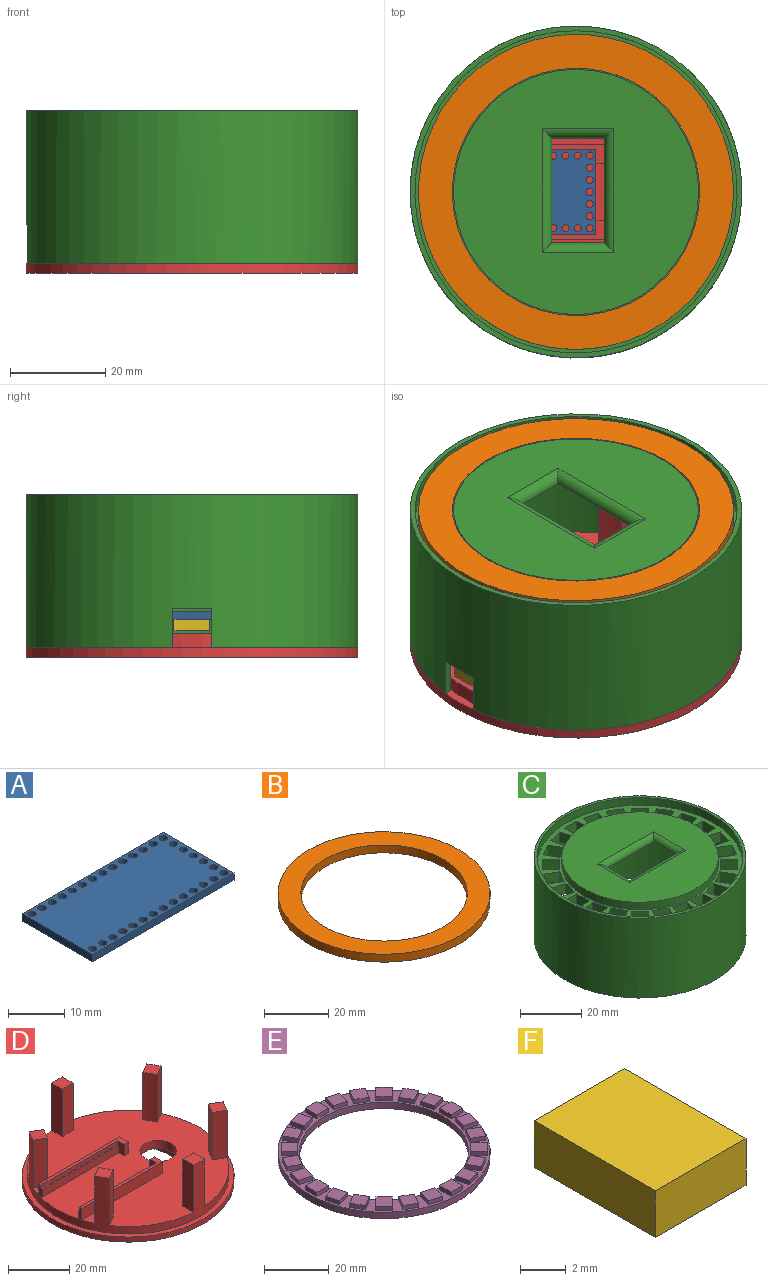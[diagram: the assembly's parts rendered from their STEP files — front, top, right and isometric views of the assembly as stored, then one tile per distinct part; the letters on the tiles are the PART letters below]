
ASSEMBLY  parts=6 mates=9
PART A: 39 faces, bbox 35.6x17.8x1.6 mm
  f0: plane 35.56x1.57mm, normal (0,1,0), area 55.8mm2, adj f1,f3,f4,f5
  f1: plane 17.78x1.57mm, normal (-1,0,0), area 27.9mm2, adj f0,f2,f4,f5
  f2: plane 35.56x1.57mm, normal (0,-1,0), area 55.8mm2, adj f1,f3,f4,f5
  f3: plane 17.78x1.57mm, normal (1,0,0), area 27.9mm2, adj f0,f2,f4,f5
  f4: plane 35.56x17.78mm, normal (0,0,1), area 573.9mm2, adj f0,f1,f2,f3,f6,f7,f8,f9
  f5: plane 35.56x17.78mm, normal (0,0,-1), area 573.9mm2, adj f0,f1,f2,f3,f6,f7,f8,f9
  f6: cylinder r=0.75mm len=1.57mm, axis (0,0,1), area 7.4mm2, adj f4,f5
  f7: cylinder r=0.75mm len=1.57mm, axis (0,0,1), area 7.4mm2, adj f4,f5
  f8: cylinder r=0.75mm len=1.57mm, axis (0,0,1), area 7.4mm2, adj f4,f5
  f9: cylinder r=0.75mm len=1.57mm, axis (0,0,1), area 7.4mm2, adj f4,f5
  f10: cylinder r=0.75mm len=1.57mm, axis (0,0,1), area 7.4mm2, adj f4,f5
  f11: cylinder r=0.75mm len=1.57mm, axis (0,0,1), area 7.4mm2, adj f4,f5
  f12: cylinder r=0.75mm len=1.57mm, axis (0,0,1), area 7.4mm2, adj f4,f5
  f13: cylinder r=0.75mm len=1.57mm, axis (0,0,1), area 7.4mm2, adj f4,f5
  f14: cylinder r=0.75mm len=1.57mm, axis (0,0,1), area 7.4mm2, adj f4,f5
  f15: cylinder r=0.75mm len=1.57mm, axis (0,0,1), area 7.4mm2, adj f4,f5
  f16: cylinder r=0.75mm len=1.57mm, axis (0,0,1), area 7.4mm2, adj f4,f5
  f17: cylinder r=0.75mm len=1.57mm, axis (0,0,1), area 7.4mm2, adj f4,f5
  f18: cylinder r=0.75mm len=1.57mm, axis (0,0,1), area 7.4mm2, adj f4,f5
  f19: cylinder r=0.75mm len=1.57mm, axis (0,0,1), area 7.4mm2, adj f4,f5
  f20: cylinder r=0.75mm len=1.57mm, axis (0,0,1), area 7.4mm2, adj f4,f5
  f21: cylinder r=0.75mm len=1.57mm, axis (0,0,1), area 7.4mm2, adj f4,f5
  f22: cylinder r=0.75mm len=1.57mm, axis (0,0,1), area 7.4mm2, adj f4,f5
  f23: cylinder r=0.75mm len=1.57mm, axis (0,0,1), area 7.4mm2, adj f4,f5
  f24: cylinder r=0.75mm len=1.57mm, axis (0,0,1), area 7.4mm2, adj f4,f5
  f25: cylinder r=0.75mm len=1.57mm, axis (0,0,1), area 7.4mm2, adj f4,f5
  f26: cylinder r=0.75mm len=1.57mm, axis (0,0,1), area 7.4mm2, adj f4,f5
  f27: cylinder r=0.75mm len=1.57mm, axis (0,0,1), area 7.4mm2, adj f4,f5
  f28: cylinder r=0.75mm len=1.57mm, axis (0,0,1), area 7.4mm2, adj f4,f5
  f29: cylinder r=0.75mm len=1.57mm, axis (0,0,1), area 7.4mm2, adj f4,f5
  f30: cylinder r=0.75mm len=1.57mm, axis (0,0,1), area 7.4mm2, adj f4,f5
  f31: cylinder r=0.75mm len=1.57mm, axis (0,0,1), area 7.4mm2, adj f4,f5
  f32: cylinder r=0.75mm len=1.57mm, axis (0,0,1), area 7.4mm2, adj f4,f5
  f33: cylinder r=0.75mm len=1.57mm, axis (0,0,1), area 7.4mm2, adj f4,f5
  f34: cylinder r=0.75mm len=1.57mm, axis (0,0,1), area 7.4mm2, adj f4,f5
  f35: cylinder r=0.75mm len=1.57mm, axis (0,0,1), area 7.4mm2, adj f4,f5
  f36: cylinder r=0.75mm len=1.57mm, axis (0,0,1), area 7.4mm2, adj f4,f5
  f37: cylinder r=0.75mm len=1.57mm, axis (0,0,1), area 7.4mm2, adj f4,f5
  f38: cylinder r=0.75mm len=1.57mm, axis (0,0,1), area 7.4mm2, adj f4,f5
PART B: 4 faces, bbox 66x66x3 mm
  f0: cylinder r=25.9mm len=51.8mm, axis (0,0,-1), area 488.2mm2, adj f2,f3
  f1: cylinder r=33mm len=66mm, axis (0,0,-1), area 622mm2, adj f2,f3
  f2: plane 66x66mm, normal (0,0,1), area 1313.8mm2, adj f0,f1
  f3: plane 66x66mm, normal (0,0,-1), area 1313.8mm2, adj f0,f1
PART C: 136 faces, bbox 69.5x69.5x32 mm
  f0: plane 39.1x29.45mm, normal (0,0,-1), area 578.4mm2, adj f115,f116,f117,f118,f119,f120,f121,f122
  f1: plane 48.3x48.3mm, normal (0,0,-1), area 691.6mm2, adj f4,f115,f116,f117,f118,f119,f120,f121
  f2: plane 51.3x51.3mm, normal (0,0,1), area 1678.2mm2, adj f107,f111,f112,f113,f114
  f3: plane 69.5x69.25mm, normal (0,0,-1), area 308mm2, adj f77,f104,f109,f110
  f4: cylinder r=24.15mm len=48.3mm, axis (0,0,-1), area 151.7mm2, adj f1,f103
  f5: plane 5.7x4mm, normal (0,-1,0), area 22.8mm2, adj f6,f101,f102,f103
  f6: plane 5.7x4mm, normal (-1,0,0), area 22.8mm2, adj f5,f7,f102,f103
  f7: plane 5.7x4mm, normal (0,1,0), area 22.8mm2, adj f6,f101,f102,f103
  f8: plane 5.51x4mm, normal (-0.26,-0.97,0), area 22.8mm2, adj f9,f78,f102,f103
  f9: plane 5.51x4mm, normal (-0.97,0.26,0), area 22.8mm2, adj f8,f10,f102,f103
  f10: plane 5.51x4mm, normal (0.26,0.97,0), area 22.8mm2, adj f9,f78,f102,f103
  f11: plane 4.94x4mm, normal (-0.5,-0.87,0), area 22.8mm2, adj f12,f79,f102,f103
  f12: plane 4.94x4mm, normal (-0.87,0.5,0), area 22.8mm2, adj f11,f13,f102,f103
  f13: plane 4.94x4mm, normal (0.5,0.87,0), area 22.8mm2, adj f12,f79,f102,f103
  f14: plane 4.03x4.03mm, normal (-0.71,-0.71,0), area 22.8mm2, adj f15,f80,f102,f103
  f15: plane 4.03x4.03mm, normal (-0.71,0.71,0), area 22.8mm2, adj f14,f16,f102,f103
  f16: plane 4.03x4.03mm, normal (0.71,0.71,0), area 22.8mm2, adj f15,f80,f102,f103
  f17: plane 4.94x4mm, normal (-0.87,-0.5,0), area 22.8mm2, adj f18,f81,f102,f103
  f18: plane 4.94x4mm, normal (-0.5,0.87,0), area 22.8mm2, adj f17,f19,f102,f103
  f19: plane 4.94x4mm, normal (0.87,0.5,0), area 22.8mm2, adj f18,f81,f102,f103
  f20: plane 5.51x4mm, normal (-0.97,-0.26,0), area 22.8mm2, adj f21,f82,f102,f103
  f21: plane 5.51x4mm, normal (-0.26,0.97,0), area 22.8mm2, adj f20,f22,f102,f103
  f22: plane 5.51x4mm, normal (0.97,0.26,0), area 22.8mm2, adj f21,f82,f102,f103
  f23: plane 5.7x4mm, normal (-1,0,0), area 22.8mm2, adj f24,f83,f102,f103
  f24: plane 5.7x4mm, normal (0,1,0), area 22.8mm2, adj f23,f25,f102,f103
  f25: plane 5.7x4mm, normal (1,0,0), area 22.8mm2, adj f24,f83,f102,f103
  f26: plane 5.51x4mm, normal (-0.97,0.26,0), area 22.8mm2, adj f27,f84,f102,f103
  f27: plane 5.51x4mm, normal (0.26,0.97,0), area 22.8mm2, adj f26,f28,f102,f103
  f28: plane 5.51x4mm, normal (0.97,-0.26,0), area 22.8mm2, adj f27,f84,f102,f103
  f29: plane 4.94x4mm, normal (-0.87,0.5,0), area 22.8mm2, adj f30,f85,f102,f103
  f30: plane 4.94x4mm, normal (0.5,0.87,0), area 22.8mm2, adj f29,f31,f102,f103
  f31: plane 4.94x4mm, normal (0.87,-0.5,0), area 22.8mm2, adj f30,f85,f102,f103
  f32: plane 4.03x4.03mm, normal (-0.71,0.71,0), area 22.8mm2, adj f33,f86,f102,f103
  f33: plane 4.03x4.03mm, normal (0.71,0.71,0), area 22.8mm2, adj f32,f34,f102,f103
  f34: plane 4.03x4.03mm, normal (0.71,-0.71,0), area 22.8mm2, adj f33,f86,f102,f103
  f35: plane 4.94x4mm, normal (-0.5,0.87,0), area 22.8mm2, adj f36,f87,f102,f103
  f36: plane 4.94x4mm, normal (0.87,0.5,0), area 22.8mm2, adj f35,f37,f102,f103
  f37: plane 4.94x4mm, normal (0.5,-0.87,0), area 22.8mm2, adj f36,f87,f102,f103
  f38: plane 5.51x4mm, normal (-0.26,0.97,0), area 22.8mm2, adj f39,f88,f102,f103
  f39: plane 5.51x4mm, normal (0.97,0.26,0), area 22.8mm2, adj f38,f40,f102,f103
  f40: plane 5.51x4mm, normal (0.26,-0.97,0), area 22.8mm2, adj f39,f88,f102,f103
  f41: plane 5.7x4mm, normal (0,1,0), area 22.8mm2, adj f42,f89,f102,f103
  f42: plane 5.7x4mm, normal (1,0,0), area 22.8mm2, adj f41,f43,f102,f103
  f43: plane 5.7x4mm, normal (0,-1,0), area 22.8mm2, adj f42,f89,f102,f103
  f44: plane 5.51x4mm, normal (0.26,0.97,0), area 22.8mm2, adj f45,f90,f102,f103
  f45: plane 5.51x4mm, normal (0.97,-0.26,0), area 22.8mm2, adj f44,f46,f102,f103
  f46: plane 5.51x4mm, normal (-0.26,-0.97,0), area 22.8mm2, adj f45,f90,f102,f103
  f47: plane 4.94x4mm, normal (0.5,0.87,0), area 22.8mm2, adj f48,f91,f102,f103
  f48: plane 4.94x4mm, normal (0.87,-0.5,0), area 22.8mm2, adj f47,f49,f102,f103
  f49: plane 4.94x4mm, normal (-0.5,-0.87,0), area 22.8mm2, adj f48,f91,f102,f103
  f50: plane 4.03x4.03mm, normal (0.71,0.71,0), area 22.8mm2, adj f51,f92,f102,f103
  f51: plane 4.03x4.03mm, normal (0.71,-0.71,0), area 22.8mm2, adj f50,f52,f102,f103
  f52: plane 4.03x4.03mm, normal (-0.71,-0.71,0), area 22.8mm2, adj f51,f92,f102,f103
  f53: plane 4.94x4mm, normal (0.87,0.5,0), area 22.8mm2, adj f54,f93,f102,f103
  f54: plane 4.94x4mm, normal (0.5,-0.87,0), area 22.8mm2, adj f53,f55,f102,f103
  f55: plane 4.94x4mm, normal (-0.87,-0.5,0), area 22.8mm2, adj f54,f93,f102,f103
  f56: plane 5.51x4mm, normal (0.97,0.26,0), area 22.8mm2, adj f57,f94,f102,f103
  f57: plane 5.51x4mm, normal (0.26,-0.97,0), area 22.8mm2, adj f56,f58,f102,f103
  f58: plane 5.51x4mm, normal (-0.97,-0.26,0), area 22.8mm2, adj f57,f94,f102,f103
  f59: plane 5.7x4mm, normal (1,0,0), area 22.8mm2, adj f60,f95,f102,f103
  f60: plane 5.7x4mm, normal (0,-1,0), area 22.8mm2, adj f59,f61,f102,f103
  f61: plane 5.7x4mm, normal (-1,0,0), area 22.8mm2, adj f60,f95,f102,f103
  f62: plane 5.51x4mm, normal (0.97,-0.26,0), area 22.8mm2, adj f63,f96,f102,f103
  f63: plane 5.51x4mm, normal (-0.26,-0.97,0), area 22.8mm2, adj f62,f64,f102,f103
  f64: plane 5.51x4mm, normal (-0.97,0.26,0), area 22.8mm2, adj f63,f96,f102,f103
  f65: plane 4.94x4mm, normal (0.87,-0.5,0), area 22.8mm2, adj f66,f97,f102,f103
  f66: plane 4.94x4mm, normal (-0.5,-0.87,0), area 22.8mm2, adj f65,f67,f102,f103
  f67: plane 4.94x4mm, normal (-0.87,0.5,0), area 22.8mm2, adj f66,f97,f102,f103
  f68: plane 4.03x4.03mm, normal (0.71,-0.71,0), area 22.8mm2, adj f69,f98,f102,f103
  f69: plane 4.03x4.03mm, normal (-0.71,-0.71,0), area 22.8mm2, adj f68,f70,f102,f103
  f70: plane 4.03x4.03mm, normal (-0.71,0.71,0), area 22.8mm2, adj f69,f98,f102,f103
  f71: plane 4.94x4mm, normal (0.5,-0.87,0), area 22.8mm2, adj f72,f99,f102,f103
  f72: plane 4.94x4mm, normal (-0.87,-0.5,0), area 22.8mm2, adj f71,f73,f102,f103
  f73: plane 4.94x4mm, normal (-0.5,0.87,0), area 22.8mm2, adj f72,f99,f102,f103
  f74: plane 5.51x4mm, normal (0.26,-0.97,0), area 22.8mm2, adj f75,f100,f102,f103
  f75: plane 5.51x4mm, normal (-0.97,-0.26,0), area 22.8mm2, adj f74,f76,f102,f103
  f76: plane 5.51x4mm, normal (-0.26,0.97,0), area 22.8mm2, adj f75,f100,f102,f103
  f77: cylinder r=34.75mm len=69.5mm, axis (0,0,-1), area 6918.7mm2, adj f3,f106,f108,f109,f110
  f78: plane 5.51x4mm, normal (0.97,-0.26,0), area 22.8mm2, adj f8,f10,f102,f103
  f79: plane 4.94x4mm, normal (0.87,-0.5,0), area 22.8mm2, adj f11,f13,f102,f103
  f80: plane 4.03x4.03mm, normal (0.71,-0.71,0), area 22.8mm2, adj f14,f16,f102,f103
  f81: plane 4.94x4mm, normal (0.5,-0.87,0), area 22.8mm2, adj f17,f19,f102,f103
  f82: plane 5.51x4mm, normal (0.26,-0.97,0), area 22.8mm2, adj f20,f22,f102,f103
  f83: plane 5.7x4mm, normal (0,-1,0), area 22.8mm2, adj f23,f25,f102,f103
  f84: plane 5.51x4mm, normal (-0.26,-0.97,0), area 22.8mm2, adj f26,f28,f102,f103
  f85: plane 4.94x4mm, normal (-0.5,-0.87,0), area 22.8mm2, adj f29,f31,f102,f103
  f86: plane 4.03x4.03mm, normal (-0.71,-0.71,0), area 22.8mm2, adj f32,f34,f102,f103
  f87: plane 4.94x4mm, normal (-0.87,-0.5,0), area 22.8mm2, adj f35,f37,f102,f103
  f88: plane 5.51x4mm, normal (-0.97,-0.26,0), area 22.8mm2, adj f38,f40,f102,f103
  f89: plane 5.7x4mm, normal (-1,0,0), area 22.8mm2, adj f41,f43,f102,f103
  f90: plane 5.51x4mm, normal (-0.97,0.26,0), area 22.8mm2, adj f44,f46,f102,f103
  f91: plane 4.94x4mm, normal (-0.87,0.5,0), area 22.8mm2, adj f47,f49,f102,f103
  f92: plane 4.03x4.03mm, normal (-0.71,0.71,0), area 22.8mm2, adj f50,f52,f102,f103
  f93: plane 4.94x4mm, normal (-0.5,0.87,0), area 22.8mm2, adj f53,f55,f102,f103
  f94: plane 5.51x4mm, normal (-0.26,0.97,0), area 22.8mm2, adj f56,f58,f102,f103
  f95: plane 5.7x4mm, normal (0,1,0), area 22.8mm2, adj f59,f61,f102,f103
  f96: plane 5.51x4mm, normal (0.26,0.97,0), area 22.8mm2, adj f62,f64,f102,f103
  f97: plane 4.94x4mm, normal (0.5,0.87,0), area 22.8mm2, adj f65,f67,f102,f103
  f98: plane 4.03x4.03mm, normal (0.71,0.71,0), area 22.8mm2, adj f68,f70,f102,f103
  f99: plane 4.94x4mm, normal (0.87,0.5,0), area 22.8mm2, adj f71,f73,f102,f103
  f100: plane 5.51x4mm, normal (0.97,0.26,0), area 22.8mm2, adj f74,f76,f102,f103
  f101: plane 5.7x4mm, normal (1,0,0), area 22.8mm2, adj f5,f7,f102,f103
  f102: plane 67.5x67.5mm, normal (0,0,1), area 731.8mm2, adj f5,f6,f7,f8,f9,f10,f11,f12
  f103: plane 66.5x66.5mm, normal (0,0,-1), area 861.2mm2, adj f4,f5,f6,f7,f8,f9,f10,f11
  f104: cylinder r=33.25mm len=66.5mm, axis (0,0,1), area 5154.7mm2, adj f3,f103,f108,f109,f110
  f105: cylinder r=33.75mm len=67.5mm, axis (0,0,-1), area 636.2mm2, adj f102,f106
  f106: plane 69.5x69.5mm, normal (0,0,1), area 215.2mm2, adj f77,f105
  f107: cylinder r=25.65mm len=51.3mm, axis (0,0,-1), area 483.5mm2, adj f2,f102
  f108: plane 8.25x1.76mm, normal (0,0,-1), area 12.4mm2, adj f77,f104,f109,f110
  f109: plane 8.25x1.51mm, normal (-1,0,0), area 12.5mm2, adj f3,f77,f104,f108
  f110: plane 8.25x1.51mm, normal (1,0,0), area 12.5mm2, adj f3,f77,f104,f108
  f111: cylinder r=2mm len=25.92mm, axis (1,0,0), area 73.4mm2, adj f2,f112,f113,f127
  f112: cylinder r=2mm len=15mm, axis (0,-1,0), area 39.1mm2, adj f2,f111,f114,f127
  f113: cylinder r=2mm len=15mm, axis (0,1,0), area 39.1mm2, adj f2,f111,f114,f127
  f114: cylinder r=2mm len=25.92mm, axis (-1,0,0), area 73.4mm2, adj f2,f112,f113,f127
  f115: plane 32x3mm, normal (0,-1,0), area 96mm2, adj f0,f1,f116,f122
  f116: cylinder r=3.55mm len=3.55mm, axis (0,0,-1), area 16.7mm2, adj f0,f1,f115,f117
  f117: plane 22.35x3mm, normal (-1,0,0), area 67.1mm2, adj f0,f1,f116,f118
  f118: cylinder r=3.55mm len=3.55mm, axis (0,0,-1), area 16.7mm2, adj f0,f1,f117,f119
  f119: plane 32x3mm, normal (0,1,0), area 96mm2, adj f0,f1,f118,f120
  f120: cylinder r=3.55mm len=3.55mm, axis (0,0,-1), area 16.7mm2, adj f0,f1,f119,f121
  f121: plane 22.35x3mm, normal (1,0,0), area 67.1mm2, adj f0,f1,f120,f122
  f122: cylinder r=3.55mm len=3.55mm, axis (0,0,-1), area 16.7mm2, adj f0,f1,f115,f121
  f123: plane 20.05x1mm, normal (-1,0,0), area 20mm2, adj f0,f124,f126,f127
  f124: plane 27.42x1mm, normal (0,1,0), area 27.4mm2, adj f0,f123,f125,f127
  f125: plane 20.05x1mm, normal (1,0,0), area 20mm2, adj f0,f124,f126,f127
  f126: plane 27.42x1mm, normal (0,-1,0), area 27.4mm2, adj f0,f123,f125,f127
  f127: plane 27.42x20.05mm, normal (0,0,-1), area 308.6mm2, adj f111,f112,f113,f114,f123,f124,f125,f126
  f128: cylinder r=1mm len=2mm, axis (0,0,-1), area 12.6mm2, adj f0,f129
  f129: plane 2x2mm, normal (0,0,-1), area 3.1mm2, adj f128
  f130: cylinder r=1mm len=2mm, axis (0,0,-1), area 12.6mm2, adj f0,f131
  f131: plane 2x2mm, normal (0,0,-1), area 3.1mm2, adj f130
  f132: cylinder r=1mm len=2mm, axis (0,0,-1), area 12.6mm2, adj f0,f133
  f133: plane 2x2mm, normal (0,0,-1), area 3.1mm2, adj f132
  f134: cylinder r=1mm len=2mm, axis (0,0,-1), area 12.6mm2, adj f0,f135
  f135: plane 2x2mm, normal (0,0,-1), area 3.1mm2, adj f134
PART D: 50 faces, bbox 69.5x69.5x24 mm
  f0: plane 66x65.81mm, normal (0,0,1), area 3027.3mm2, adj f4,f5,f6,f7,f9,f10,f11,f13
  f1: cylinder r=34.75mm len=69.5mm, axis (0,0,-1), area 436.7mm2, adj f2,f3
  f2: plane 69.5x69.5mm, normal (0,0,1), area 372.5mm2, adj f1,f4
  f3: plane 69.5x69.5mm, normal (0,0,-1), area 2537mm2, adj f1,f47
  f4: cylinder r=33mm len=66mm, axis (0,0,-1), area 1192.6mm2, adj f0,f2,f6,f7,f8,f9,f11,f12
  f5: cylinder r=28mm len=19mm, axis (0,0,-1), area 95.1mm2, adj f0,f6,f7,f8
  f6: plane 19x5.02mm, normal (1,0,0), area 95.3mm2, adj f0,f4,f5,f8
  f7: plane 19x5.02mm, normal (-1,0,0), area 95.3mm2, adj f0,f4,f5,f8
  f8: plane 5.11x5mm, normal (0,0,1), area 25mm2, adj f4,f5,f6,f7
  f9: plane 19x4.35mm, normal (-0.5,-0.87,0), area 95.3mm2, adj f0,f4,f10,f12
  f10: cylinder r=28mm len=19mm, axis (0,0,-1), area 95.1mm2, adj f0,f9,f11,f12
  f11: plane 19x4.35mm, normal (0.5,0.87,0), area 95.3mm2, adj f0,f4,f10,f12
  f12: plane 6.85x6.84mm, normal (0,0,1), area 25mm2, adj f4,f9,f10,f11
  f13: plane 19x4.35mm, normal (0.5,-0.87,0), area 95.3mm2, adj f0,f4,f14,f16
  f14: cylinder r=28mm len=19mm, axis (0,0,-1), area 95.1mm2, adj f0,f13,f15,f16
  f15: plane 19x4.35mm, normal (-0.5,0.87,0), area 95.3mm2, adj f0,f4,f14,f16
  f16: plane 6.85x6.84mm, normal (0,0,1), area 25mm2, adj f4,f13,f14,f15
  f17: plane 19x5.02mm, normal (1,0,0), area 95.3mm2, adj f0,f4,f18,f20
  f18: cylinder r=28mm len=19mm, axis (0,0,-1), area 95.1mm2, adj f0,f17,f19,f20
  f19: plane 19x5.02mm, normal (-1,0,0), area 95.3mm2, adj f0,f4,f18,f20
  f20: plane 5.11x5mm, normal (0,0,1), area 25mm2, adj f4,f17,f18,f19
  f21: plane 19x4.35mm, normal (0.5,0.87,0), area 95.3mm2, adj f0,f4,f22,f24
  f22: cylinder r=28mm len=19mm, axis (0,0,-1), area 95.1mm2, adj f0,f21,f23,f24
  f23: plane 19x4.35mm, normal (-0.5,-0.87,0), area 95.3mm2, adj f0,f4,f22,f24
  f24: plane 6.85x6.84mm, normal (0,0,1), area 25mm2, adj f4,f21,f22,f23
  f25: plane 19x4.35mm, normal (-0.5,0.87,0), area 95.3mm2, adj f0,f4,f26,f28
  f26: cylinder r=28mm len=19mm, axis (0,0,-1), area 95.1mm2, adj f0,f25,f27,f28
  f27: plane 19x4.35mm, normal (0.5,-0.87,0), area 95.3mm2, adj f0,f4,f26,f28
  f28: plane 6.85x6.84mm, normal (0,0,1), area 25mm2, adj f4,f25,f26,f27
  f29: plane 37.6x4.57mm, normal (0,1,0), area 171.8mm2, adj f0,f30,f38,f45
  f30: plane 4.57x1.61mm, normal (-1,0,0), area 6.5mm2, adj f0,f29,f31,f32,f37,f38
  f31: plane 35.6x3mm, normal (0,-1,0), area 106.8mm2, adj f0,f30,f32,f44
  f32: plane 35.6x0.54mm, normal (0,0,1), area 19.1mm2, adj f30,f31,f37,f44
  f33: plane 35.6x3mm, normal (0,1,0), area 106.8mm2, adj f0,f34,f36,f41
  f34: plane 4.57x1.61mm, normal (-1,0,0), area 6.6mm2, adj f0,f33,f35,f36,f39,f40
  f35: plane 37.6x4.57mm, normal (0,-1,0), area 171.8mm2, adj f0,f34,f40,f42
  f36: plane 35.6x0.46mm, normal (0,0,1), area 16.5mm2, adj f33,f34,f39,f41
  f37: plane 35.6x1.57mm, normal (0,-1,0), area 55.9mm2, adj f30,f32,f38,f44
  f38: plane 37.6x4mm, normal (0,0,1), area 46.2mm2, adj f29,f30,f37,f44,f45,f46
  f39: plane 35.6x1.57mm, normal (0,1,0), area 55.9mm2, adj f34,f36,f40,f41
  f40: plane 37.6x4mm, normal (0,0,1), area 48.8mm2, adj f34,f35,f39,f41,f42,f43
  f41: plane 4.57x2.85mm, normal (-1,0,0), area 11.7mm2, adj f0,f33,f36,f39,f40,f43
  f42: plane 4.57x4mm, normal (1,0,0), area 18.3mm2, adj f0,f35,f40,f43
  f43: plane 4.57x2mm, normal (0,1,0), area 9.1mm2, adj f0,f40,f41,f42
  f44: plane 4.57x2.93mm, normal (-1,0,0), area 11.8mm2, adj f0,f31,f32,f37,f38,f46
  f45: plane 4.57x4mm, normal (1,0,0), area 18.3mm2, adj f0,f29,f38,f46
  f46: plane 4.57x2mm, normal (0,-1,0), area 9.1mm2, adj f0,f38,f44,f45
  f47: cylinder r=20mm len=40mm, axis (0,0,-1), area 219.9mm2, adj f3,f48
  f48: plane 40x40mm, normal (0,0,-1), area 1143.5mm2, adj f47,f49
  f49: cylinder r=6mm len=12mm, axis (0,0,-1), area 122.5mm2, adj f0,f48
PART E: 124 faces, bbox 65.6x65.6x4 mm
  f0: plane 65.6x65.6mm, normal (0,0,1), area 631.6mm2, adj f1,f2,f4,f5,f6,f7,f9,f10
  f1: cylinder r=26.15mm len=52.3mm, axis (0,0,-1), area 394.3mm2, adj f0,f3
  f2: cylinder r=32.8mm len=65.6mm, axis (0,0,-1), area 494.6mm2, adj f0,f3
  f3: plane 65.6x65.6mm, normal (0,0,-1), area 1231.6mm2, adj f1,f2
  f4: plane 5x1.6mm, normal (0,1,0), area 8mm2, adj f0,f5,f7,f8
  f5: plane 5x1.6mm, normal (-1,0,0), area 8mm2, adj f0,f4,f6,f8
  f6: plane 5x1.6mm, normal (0,-1,0), area 8mm2, adj f0,f5,f7,f8
  f7: plane 5x1.6mm, normal (1,0,0), area 8mm2, adj f0,f4,f6,f8
  f8: plane 5x5mm, normal (0,0,1), area 25mm2, adj f4,f5,f6,f7
  f9: plane 4.83x1.6mm, normal (-0.26,0.97,0), area 8mm2, adj f0,f10,f12,f13
  f10: plane 4.83x1.6mm, normal (-0.97,-0.26,0), area 8mm2, adj f0,f9,f11,f13
  f11: plane 4.83x1.6mm, normal (0.26,-0.97,0), area 8mm2, adj f0,f10,f12,f13
  f12: plane 4.83x1.6mm, normal (0.97,0.26,0), area 8mm2, adj f0,f9,f11,f13
  f13: plane 6.12x6.12mm, normal (0,0,1), area 25mm2, adj f9,f10,f11,f12
  f14: plane 4.33x2.5mm, normal (-0.5,0.87,0), area 8mm2, adj f0,f15,f17,f18
  f15: plane 4.33x2.5mm, normal (-0.87,-0.5,0), area 8mm2, adj f0,f14,f16,f18
  f16: plane 4.33x2.5mm, normal (0.5,-0.87,0), area 8mm2, adj f0,f15,f17,f18
  f17: plane 4.33x2.5mm, normal (0.87,0.5,0), area 8mm2, adj f0,f14,f16,f18
  f18: plane 6.83x6.83mm, normal (0,0,1), area 25mm2, adj f14,f15,f16,f17
  f19: plane 3.54x3.54mm, normal (-0.71,0.71,0), area 8mm2, adj f0,f20,f22,f23
  f20: plane 3.54x3.54mm, normal (-0.71,-0.71,0), area 8mm2, adj f0,f19,f21,f23
  f21: plane 3.54x3.54mm, normal (0.71,-0.71,0), area 8mm2, adj f0,f20,f22,f23
  f22: plane 3.54x3.54mm, normal (0.71,0.71,0), area 8mm2, adj f0,f19,f21,f23
  f23: plane 7.07x7.07mm, normal (0,0,1), area 25mm2, adj f19,f20,f21,f22
  f24: plane 4.33x2.5mm, normal (-0.87,0.5,0), area 8mm2, adj f0,f25,f27,f28
  f25: plane 4.33x2.5mm, normal (-0.5,-0.87,0), area 8mm2, adj f0,f24,f26,f28
  f26: plane 4.33x2.5mm, normal (0.87,-0.5,0), area 8mm2, adj f0,f25,f27,f28
  f27: plane 4.33x2.5mm, normal (0.5,0.87,0), area 8mm2, adj f0,f24,f26,f28
  f28: plane 6.83x6.83mm, normal (0,0,1), area 25mm2, adj f24,f25,f26,f27
  f29: plane 4.83x1.6mm, normal (-0.97,0.26,0), area 8mm2, adj f0,f30,f32,f33
  f30: plane 4.83x1.6mm, normal (-0.26,-0.97,0), area 8mm2, adj f0,f29,f31,f33
  f31: plane 4.83x1.6mm, normal (0.97,-0.26,0), area 8mm2, adj f0,f30,f32,f33
  f32: plane 4.83x1.6mm, normal (0.26,0.97,0), area 8mm2, adj f0,f29,f31,f33
  f33: plane 6.12x6.12mm, normal (0,0,1), area 25mm2, adj f29,f30,f31,f32
  f34: plane 5x1.6mm, normal (-1,0,0), area 8mm2, adj f0,f35,f37,f38
  f35: plane 5x1.6mm, normal (0,-1,0), area 8mm2, adj f0,f34,f36,f38
  f36: plane 5x1.6mm, normal (1,0,0), area 8mm2, adj f0,f35,f37,f38
  f37: plane 5x1.6mm, normal (0,1,0), area 8mm2, adj f0,f34,f36,f38
  f38: plane 5x5mm, normal (0,0,1), area 25mm2, adj f34,f35,f36,f37
  f39: plane 4.83x1.6mm, normal (-0.97,-0.26,0), area 8mm2, adj f0,f40,f42,f43
  f40: plane 4.83x1.6mm, normal (0.26,-0.97,0), area 8mm2, adj f0,f39,f41,f43
  f41: plane 4.83x1.6mm, normal (0.97,0.26,0), area 8mm2, adj f0,f40,f42,f43
  f42: plane 4.83x1.6mm, normal (-0.26,0.97,0), area 8mm2, adj f0,f39,f41,f43
  f43: plane 6.12x6.12mm, normal (0,0,1), area 25mm2, adj f39,f40,f41,f42
  f44: plane 4.33x2.5mm, normal (-0.87,-0.5,0), area 8mm2, adj f0,f45,f47,f48
  f45: plane 4.33x2.5mm, normal (0.5,-0.87,0), area 8mm2, adj f0,f44,f46,f48
  f46: plane 4.33x2.5mm, normal (0.87,0.5,0), area 8mm2, adj f0,f45,f47,f48
  f47: plane 4.33x2.5mm, normal (-0.5,0.87,0), area 8mm2, adj f0,f44,f46,f48
  f48: plane 6.83x6.83mm, normal (0,0,1), area 25mm2, adj f44,f45,f46,f47
  f49: plane 3.54x3.54mm, normal (-0.71,-0.71,0), area 8mm2, adj f0,f50,f52,f53
  f50: plane 3.54x3.54mm, normal (0.71,-0.71,0), area 8mm2, adj f0,f49,f51,f53
  f51: plane 3.54x3.54mm, normal (0.71,0.71,0), area 8mm2, adj f0,f50,f52,f53
  f52: plane 3.54x3.54mm, normal (-0.71,0.71,0), area 8mm2, adj f0,f49,f51,f53
  f53: plane 7.07x7.07mm, normal (0,0,1), area 25mm2, adj f49,f50,f51,f52
  f54: plane 4.33x2.5mm, normal (-0.5,-0.87,0), area 8mm2, adj f0,f55,f57,f58
  f55: plane 4.33x2.5mm, normal (0.87,-0.5,0), area 8mm2, adj f0,f54,f56,f58
  f56: plane 4.33x2.5mm, normal (0.5,0.87,0), area 8mm2, adj f0,f55,f57,f58
  f57: plane 4.33x2.5mm, normal (-0.87,0.5,0), area 8mm2, adj f0,f54,f56,f58
  f58: plane 6.83x6.83mm, normal (0,0,1), area 25mm2, adj f54,f55,f56,f57
  f59: plane 4.83x1.6mm, normal (-0.26,-0.97,0), area 8mm2, adj f0,f60,f62,f63
  f60: plane 4.83x1.6mm, normal (0.97,-0.26,0), area 8mm2, adj f0,f59,f61,f63
  f61: plane 4.83x1.6mm, normal (0.26,0.97,0), area 8mm2, adj f0,f60,f62,f63
  f62: plane 4.83x1.6mm, normal (-0.97,0.26,0), area 8mm2, adj f0,f59,f61,f63
  f63: plane 6.12x6.12mm, normal (0,0,1), area 25mm2, adj f59,f60,f61,f62
  f64: plane 5x1.6mm, normal (0,-1,0), area 8mm2, adj f0,f65,f67,f68
  f65: plane 5x1.6mm, normal (1,0,0), area 8mm2, adj f0,f64,f66,f68
  f66: plane 5x1.6mm, normal (0,1,0), area 8mm2, adj f0,f65,f67,f68
  f67: plane 5x1.6mm, normal (-1,0,0), area 8mm2, adj f0,f64,f66,f68
  f68: plane 5x5mm, normal (0,0,1), area 25mm2, adj f64,f65,f66,f67
  f69: plane 4.83x1.6mm, normal (0.26,-0.97,0), area 8mm2, adj f0,f70,f72,f73
  f70: plane 4.83x1.6mm, normal (0.97,0.26,0), area 8mm2, adj f0,f69,f71,f73
  f71: plane 4.83x1.6mm, normal (-0.26,0.97,0), area 8mm2, adj f0,f70,f72,f73
  f72: plane 4.83x1.6mm, normal (-0.97,-0.26,0), area 8mm2, adj f0,f69,f71,f73
  f73: plane 6.12x6.12mm, normal (0,0,1), area 25mm2, adj f69,f70,f71,f72
  f74: plane 4.33x2.5mm, normal (0.5,-0.87,0), area 8mm2, adj f0,f75,f77,f78
  f75: plane 4.33x2.5mm, normal (0.87,0.5,0), area 8mm2, adj f0,f74,f76,f78
  f76: plane 4.33x2.5mm, normal (-0.5,0.87,0), area 8mm2, adj f0,f75,f77,f78
  f77: plane 4.33x2.5mm, normal (-0.87,-0.5,0), area 8mm2, adj f0,f74,f76,f78
  f78: plane 6.83x6.83mm, normal (0,0,1), area 25mm2, adj f74,f75,f76,f77
  f79: plane 3.54x3.54mm, normal (0.71,-0.71,0), area 8mm2, adj f0,f80,f82,f83
  f80: plane 3.54x3.54mm, normal (0.71,0.71,0), area 8mm2, adj f0,f79,f81,f83
  f81: plane 3.54x3.54mm, normal (-0.71,0.71,0), area 8mm2, adj f0,f80,f82,f83
  f82: plane 3.54x3.54mm, normal (-0.71,-0.71,0), area 8mm2, adj f0,f79,f81,f83
  f83: plane 7.07x7.07mm, normal (0,0,1), area 25mm2, adj f79,f80,f81,f82
  f84: plane 4.33x2.5mm, normal (0.87,-0.5,0), area 8mm2, adj f0,f85,f87,f88
  f85: plane 4.33x2.5mm, normal (0.5,0.87,0), area 8mm2, adj f0,f84,f86,f88
  f86: plane 4.33x2.5mm, normal (-0.87,0.5,0), area 8mm2, adj f0,f85,f87,f88
  f87: plane 4.33x2.5mm, normal (-0.5,-0.87,0), area 8mm2, adj f0,f84,f86,f88
  f88: plane 6.83x6.83mm, normal (0,0,1), area 25mm2, adj f84,f85,f86,f87
  f89: plane 4.83x1.6mm, normal (0.97,-0.26,0), area 8mm2, adj f0,f90,f92,f93
  f90: plane 4.83x1.6mm, normal (0.26,0.97,0), area 8mm2, adj f0,f89,f91,f93
  f91: plane 4.83x1.6mm, normal (-0.97,0.26,0), area 8mm2, adj f0,f90,f92,f93
  f92: plane 4.83x1.6mm, normal (-0.26,-0.97,0), area 8mm2, adj f0,f89,f91,f93
  f93: plane 6.12x6.12mm, normal (0,0,1), area 25mm2, adj f89,f90,f91,f92
  f94: plane 5x1.6mm, normal (1,0,0), area 8mm2, adj f0,f95,f97,f98
  f95: plane 5x1.6mm, normal (0,1,0), area 8mm2, adj f0,f94,f96,f98
  f96: plane 5x1.6mm, normal (-1,0,0), area 8mm2, adj f0,f95,f97,f98
  f97: plane 5x1.6mm, normal (0,-1,0), area 8mm2, adj f0,f94,f96,f98
  f98: plane 5x5mm, normal (0,0,1), area 25mm2, adj f94,f95,f96,f97
  f99: plane 4.83x1.6mm, normal (0.97,0.26,0), area 8mm2, adj f0,f100,f102,f103
  f100: plane 4.83x1.6mm, normal (-0.26,0.97,0), area 8mm2, adj f0,f99,f101,f103
  f101: plane 4.83x1.6mm, normal (-0.97,-0.26,0), area 8mm2, adj f0,f100,f102,f103
  f102: plane 4.83x1.6mm, normal (0.26,-0.97,0), area 8mm2, adj f0,f99,f101,f103
  f103: plane 6.12x6.12mm, normal (0,0,1), area 25mm2, adj f99,f100,f101,f102
  f104: plane 4.33x2.5mm, normal (0.87,0.5,0), area 8mm2, adj f0,f105,f107,f108
  f105: plane 4.33x2.5mm, normal (-0.5,0.87,0), area 8mm2, adj f0,f104,f106,f108
  f106: plane 4.33x2.5mm, normal (-0.87,-0.5,0), area 8mm2, adj f0,f105,f107,f108
  f107: plane 4.33x2.5mm, normal (0.5,-0.87,0), area 8mm2, adj f0,f104,f106,f108
  f108: plane 6.83x6.83mm, normal (0,0,1), area 25mm2, adj f104,f105,f106,f107
  f109: plane 3.54x3.54mm, normal (0.71,0.71,0), area 8mm2, adj f0,f110,f112,f113
  f110: plane 3.54x3.54mm, normal (-0.71,0.71,0), area 8mm2, adj f0,f109,f111,f113
  f111: plane 3.54x3.54mm, normal (-0.71,-0.71,0), area 8mm2, adj f0,f110,f112,f113
  f112: plane 3.54x3.54mm, normal (0.71,-0.71,0), area 8mm2, adj f0,f109,f111,f113
  f113: plane 7.07x7.07mm, normal (0,0,1), area 25mm2, adj f109,f110,f111,f112
  f114: plane 4.33x2.5mm, normal (0.5,0.87,0), area 8mm2, adj f0,f115,f117,f118
  f115: plane 4.33x2.5mm, normal (-0.87,0.5,0), area 8mm2, adj f0,f114,f116,f118
  f116: plane 4.33x2.5mm, normal (-0.5,-0.87,0), area 8mm2, adj f0,f115,f117,f118
  f117: plane 4.33x2.5mm, normal (0.87,-0.5,0), area 8mm2, adj f0,f114,f116,f118
  f118: plane 6.83x6.83mm, normal (0,0,1), area 25mm2, adj f114,f115,f116,f117
  f119: plane 4.83x1.6mm, normal (0.26,0.97,0), area 8mm2, adj f0,f120,f122,f123
  f120: plane 4.83x1.6mm, normal (-0.97,0.26,0), area 8mm2, adj f0,f119,f121,f123
  f121: plane 4.83x1.6mm, normal (-0.26,-0.97,0), area 8mm2, adj f0,f120,f122,f123
  f122: plane 4.83x1.6mm, normal (0.97,-0.26,0), area 8mm2, adj f0,f119,f121,f123
  f123: plane 6.12x6.12mm, normal (0,0,1), area 25mm2, adj f119,f120,f121,f122
PART F: 6 faces, bbox 5.6x7.5x2.5 mm
  f0: plane 5.6x2.5mm, normal (0,1,0), area 14mm2, adj f1,f3,f4,f5
  f1: plane 7.5x2.5mm, normal (-1,0,0), area 18.7mm2, adj f0,f2,f4,f5
  f2: plane 5.6x2.5mm, normal (0,-1,0), area 14mm2, adj f1,f3,f4,f5
  f3: plane 7.5x2.5mm, normal (1,0,0), area 18.7mm2, adj f0,f2,f4,f5
  f4: plane 7.5x5.6mm, normal (0,0,1), area 42mm2, adj f0,f1,f2,f3
  f5: plane 7.5x5.6mm, normal (0,0,-1), area 42mm2, adj f0,f1,f2,f3
PLACE A rot(axis=(1,0,0),180deg) t=(-45.88,-12.1,9.45)mm
PLACE B t=(-32.26,-12.13,30.9)mm
PLACE C rot(axis=(0,0,1),90deg) t=(-32.26,-12.13,26.9)mm
PLACE D t=(-32.26,-12.13,-0.12)mm fixed
PLACE E rot(axis=(0,0,-1),0deg) t=(-32.26,-12.13,23.88)mm
PLACE F rot(axis=(1,0,0),180deg) t=(-45.88,-12.1,9.45)mm
MATE planar C.f102 <-> B.f1  axis (0,0,1) through (-16.23,-39.9,30.9)mm
MATE cylindrical C.f104 <-> D.f4  axis (0,0,1) through (-32.26,-12.13,1.9)mm
MATE parallel C.f109 <-> F.f2  axis (0,-1,0) through (-66,-8.01,6.03)mm
MATE planar D.f32 <-> A.f4  axis (0,0,1) through (-63.7,-3.47,7.88)mm
MATE planar D.f44 <-> A.f3  axis (-1,0,0) through (-28.1,-4.83,7.27)mm
MATE planar E.f2 <-> D.f16  axis (0,0,-1) through (-32.26,-12.13,23.88)mm
MATE cylindrical B.f0 <-> C.f107  axis (0,0,-1) through (-32.26,-12.13,32.4)mm
MATE cylindrical E.f2 <-> D.f4  axis (0,0,-1) through (-32.26,-12.13,25.08)mm
MATE planar D.f39 <-> A.f0  axis (0,1,0) through (-45.9,-20.99,8.66)mm
